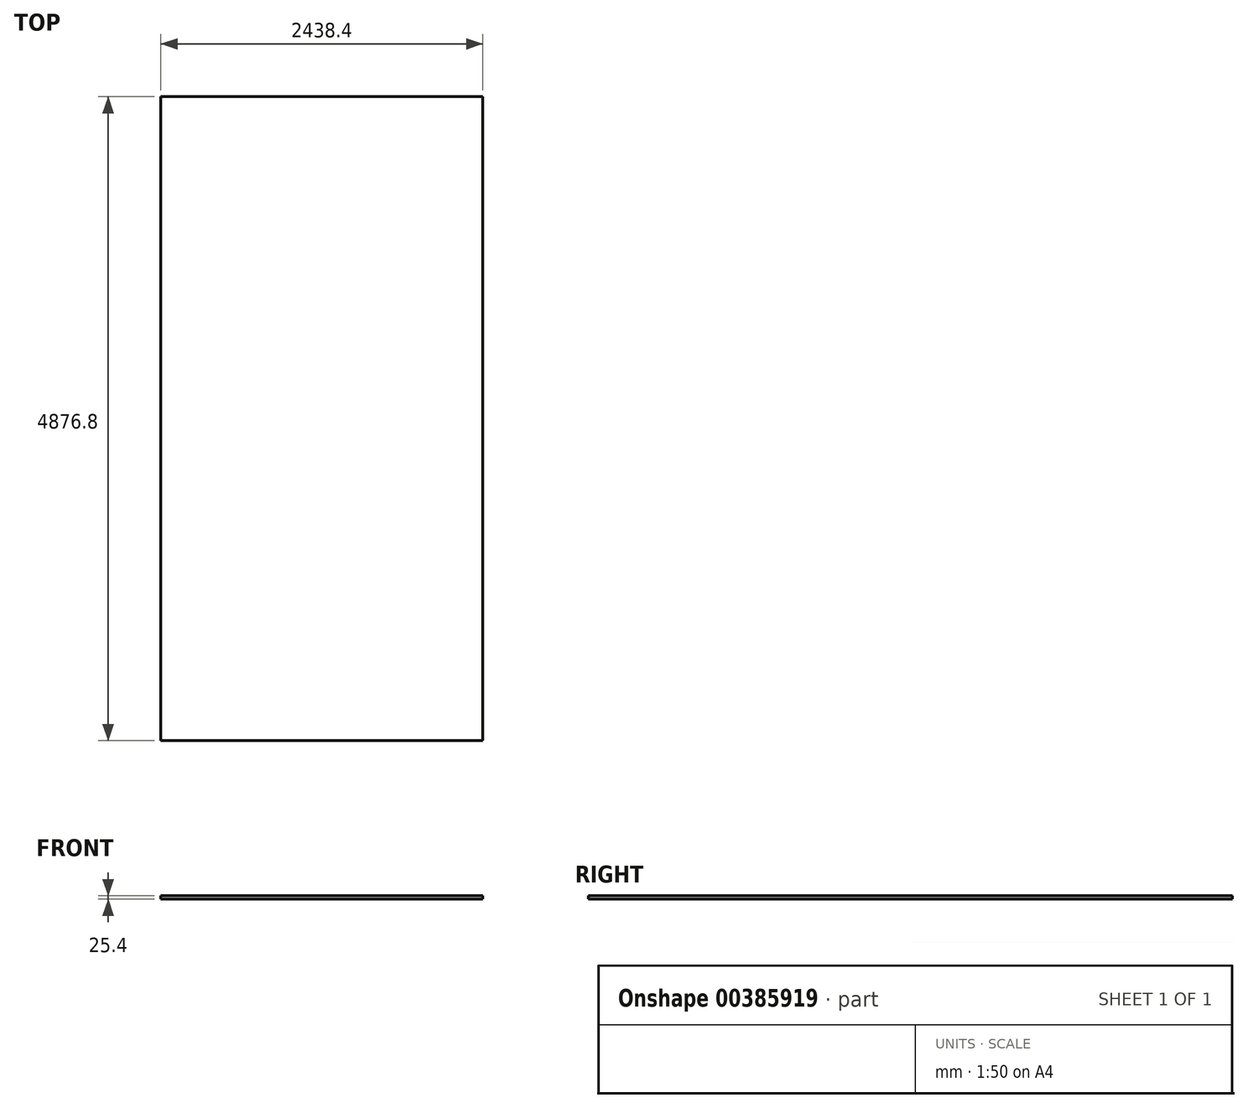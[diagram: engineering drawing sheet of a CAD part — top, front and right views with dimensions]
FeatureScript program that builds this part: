
annotation { "Feature Type Name" : "Feature", "Feature Type Description" : "" }
export const myFeature = defineFeature(function(context is Context, id is Id, definition is map)
    precondition{}
    {
        {
            var Q0;
            Q0=qCreatedBy(makeId("Top.planeOp"),FACE);
            var sketch = newSketch(context, id + "F0", { "sketchPlane" : qUnion([Q0])});
            skLineSegment(sketch, "E0.bottom", {"start": v(1219.2, -2438.4) * mm, "end": v(-1219.2, -2438.4) * mm});
            skLineSegment(sketch, "E0.top", {"start": v(1219.2, 2438.4) * mm, "end": v(-1219.2, 2438.4) * mm});
            skLineSegment(sketch, "E0.left", {"start": v(1219.2, -2438.4) * mm, "end": v(1219.2, 2438.4) * mm});
            skLineSegment(sketch, "E0.right", {"start": v(-1219.2, -2438.4) * mm, "end": v(-1219.2, 2438.4) * mm});
            skPoint(sketch, "E0.middle", {"position": v(0, 0) * mm});
            skSolve(sketch);
        }
        {
            var Q0;
            Q0 = qSketchRegion(id + "F0", true);
            extrude(context, id + "F1", {"entities" : qUnion([Q0]), "depth" : 25.4 * mm});
        }
    });
